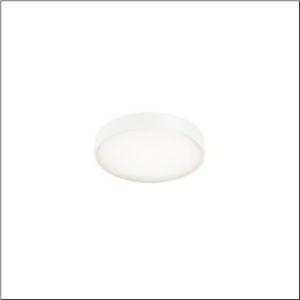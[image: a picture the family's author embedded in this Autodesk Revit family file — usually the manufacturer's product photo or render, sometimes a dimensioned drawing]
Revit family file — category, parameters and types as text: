
# Revit family: round_21_s_51mr34fd0321w
name_source: partatom
category: Lighting Fixtures
units: mm (PartAtom-declared; Revit-internal decimal feet)

## family parameters
Cut with Voids When Loaded = No
Host = Face
Light Source = No
Part Type = Normal
Room Calculation Point = No
Round Connector Dimension = Use Diameter
Shared = No

## types (1)
- Round 21 S (1 x LED, 3750 lm, 30.3 W, 3000K)
    Apparent Load = 30 VA
    CIE Flux Codes = 49 80 96 100 100
    Color Rendering = 80
    Color Temperature = 3000K
    Default Elevation = 1800 mm
    Description = Round 21 S, wall and ceiling luminaire, primary optical cover: cover, of PMMA, opal, light emission: direct distribution, primary light characteristic: symmetric, installation type: suspended mounting, surface-mounted, LED, rated luminous flux: 3.750lm, luminous efficacy: 124lm/W, light colour: 830, colour temperature: 3000K, control gear: DALI 2, with terminal, 5-pole, mains connection: 230V, AC, 50/60Hz, rated input power: 30.3W, housing, of aluminium, coated, white, diameter: 400mm, height: 62mm, protection rating (complete): IP40, insulation class (complete): insulation class I (protective earthing), certification: CE, impact resistance: IK04, permissible operating ambient temperature: -10..+35°C, packaging unit: 1 piece
    Height = 87 mm
    Lamp = 1 x LED
    Lamp Light Flux = 3750 lm
    Lamp Power = 30.3 W
    Lamp count = 1
    Length = 400 mm
    Luminous efficacy = 124 lm/W
    Manufacturer = Siteco
    ModVariant = No
    Model = 51MR34FD0321W
    Mounting Place = Ceiling
    Mounting Type = Surface mounted
    Number of Poles = 1
    OnlyDefault = Yes
    Power Factor = 1
    Product Name = Round 21 S
    Product group = wall and ceiling luminaire
    ProductGroupID = 304
    Protection Class = Protection class I
    Protection Degree = IP 40
    RLX_Detail_Level = 1
    RLX_Emergency_Light_Flux = 0 lm
    RLX_Emergency_Type = 0
    RLX_Emergency_Type_DB = No
    RlxData = <blob elided: 9501 chars, md5=c25c7f29>
    Socket = socket
    Standby Power = 0 W
    System Light Flux = 3750 lm
    System Power = 30 W
    Type Comments = Product without accessories
    Type Image = l_1258307.jpg
    URL = http://relux.com
    VarID = ---
    Voltage = 0 V
    Weight = 0.00 kg
    Width = 0 mm  [stored 0 ft]

note: [stored X ft] marks values corroborated as IEEE doubles in the binary element streams (Revit-internal decimal feet)

## geometry (parser evidence)
native form markers: Sweep x10
no freeform markers — native parametric forms only
